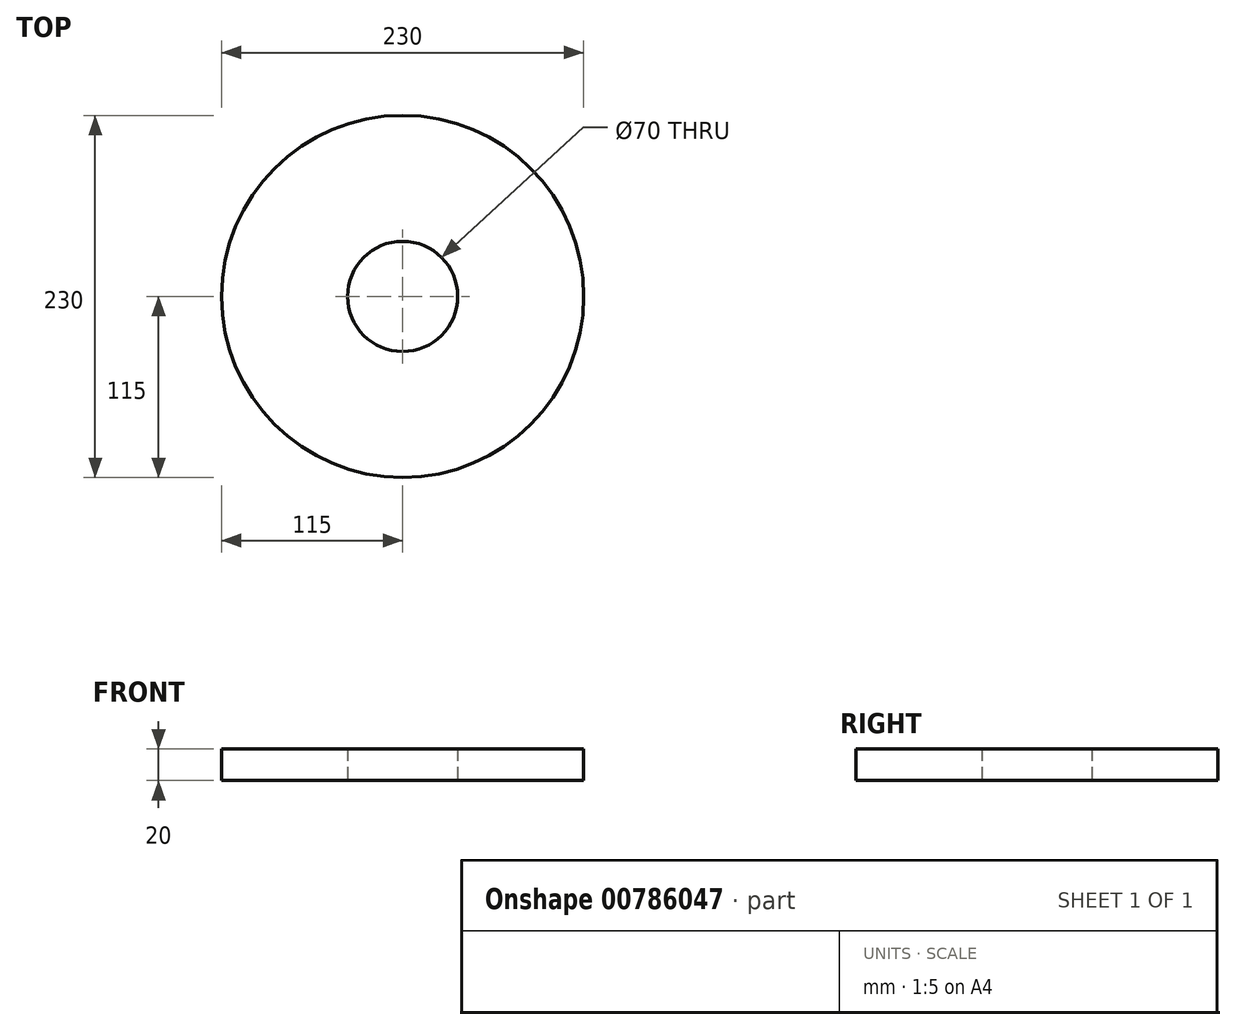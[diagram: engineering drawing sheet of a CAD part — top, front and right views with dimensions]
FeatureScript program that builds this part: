
annotation { "Feature Type Name" : "Feature", "Feature Type Description" : "" }
export const myFeature = defineFeature(function(context is Context, id is Id, definition is map)
    precondition{}
    {
        {
            var Q0;
            Q0=qCreatedBy(makeId("Top.planeOp"),FACE);
            var sketch = newSketch(context, id + "F0", { "sketchPlane" : qUnion([Q0])});
            skCircle(sketch, "E0", {"center": v(0, 0) * mm, "radius": 115 * mm});
            skCircle(sketch, "E1", {"center": v(0, 0) * mm, "radius": 35 * mm});
            skSolve(sketch);
        }
        {
            var Q0;
            Q0=qSketchRegion(id+"F0",true);
            extrude(context, id + "F1", {"entities" : qUnion([Q0]), "depth" : 20 * mm});
        }
    });
